# Revit family: Sanitary_Storage_Alterna-vanity-unit-with-ceramic-b
name_source: partatom
category: Furniture
units: mm (PartAtom-declared; Revit-internal decimal feet)

## family parameters
Always vertical = No
Cut with Voids When Loaded = No
OmniClass Number = 23.40.20.00
OmniClass Title = General Furniture and Specialties
Room Calculation Point = No
Shared = No
Work Plane-Based = No

## types (1)
- Default
    BIMobject category = Storage
    BIMobject category code = sanitary-storage
    BIMobject main category = Sanitary
    BIMobject main category code = sanitary
    BOSUseNativeGeometries = 1
    Brand url = http://www.dahl.se
    Default Elevation = 0' - 0"
    Design country = Italy
    Edition number = 1
    IFC Classification = Furnishing Element
    Manufacturer country = Italy
    Manufacturer name = Alterna
    Material main = MDF board
    Material secondary = Ceramics
    Product Guid = ecb6dac6-6f59-49e0-b11b-6e8711c4cbf1
    Product SKU = AllDaycolor_underskap_porslin
    Product data url = https://bimobject.com
    Product family = Sanitet
    Product group = Badrumsmöbler
    Product name = All Day Color vanity unit with ceramic basin
    Product url = https://www.rskdatabasen.se
    QR code = http://bimobject.com

## geometry (parser evidence)
native form markers: Sweep x3
no freeform markers — native parametric forms only
